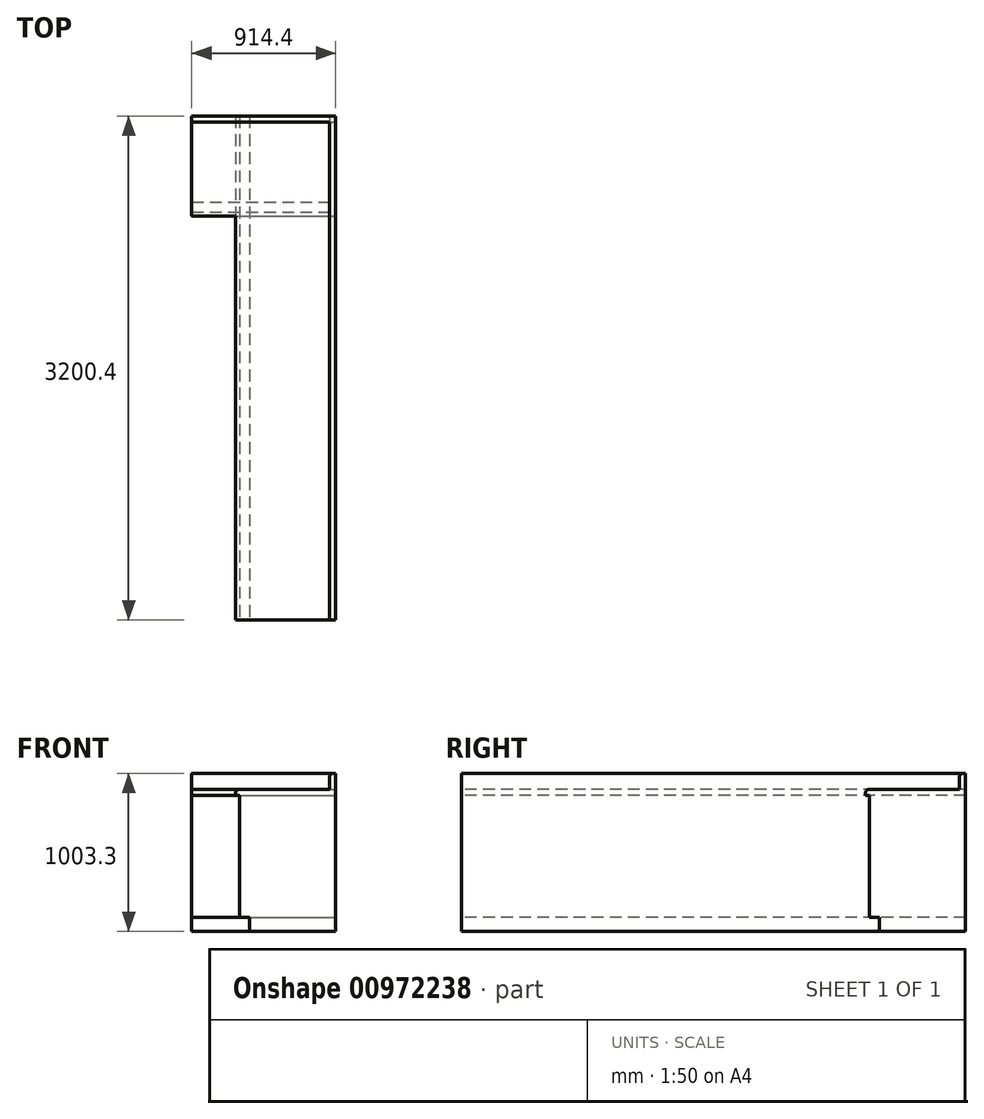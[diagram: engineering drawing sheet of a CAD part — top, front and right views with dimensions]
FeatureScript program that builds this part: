
annotation { "Feature Type Name" : "Feature", "Feature Type Description" : "" }
export const myFeature = defineFeature(function(context is Context, id is Id, definition is map)
    precondition{}
    {
        {
            var Q0;
            Q0=qCreatedBy(makeId("Front.planeOp"),FACE);
            var sketch = newSketch(context, id + "F0", { "sketchPlane" : qUnion([Q0])});
            skLineSegment(sketch, "E0", {"start": v(0, 0) * mm, "end": v(0, 1003.3) * mm});
            skLineSegment(sketch, "E1", {"start": v(0, 1003.3) * mm, "end": v(-19.05, 1003.3) * mm});
            skLineSegment(sketch, "E2", {"start": v(0, 0) * mm, "end": v(-546.1, 0) * mm});
            skLineSegment(sketch, "E3", {"start": v(-546.1, 0) * mm, "end": v(-546.1, 88.9) * mm});
            skLineSegment(sketch, "E4", {"start": v(-546.1, 88.9) * mm, "end": v(-609.6, 88.9) * mm});
            skLineSegment(sketch, "E5", {"start": v(-609.6, 88.9) * mm, "end": v(-609.6, 863.6) * mm});
            skLineSegment(sketch, "E6", {"start": v(-609.6, 863.6) * mm, "end": v(-635, 863.6) * mm});
            skLineSegment(sketch, "E7", {"start": v(-635, 863.6) * mm, "end": v(-635, 882.65) * mm});
            skArc(sketch, "E8", {"start": v(-615.95, 901.7) * mm, "mid": v(-629.42, 896.12) * mm, "end": v(-635, 882.65) * mm});
            skArc(sketch, "E9", {"start": v(-19.05, 1003.3) * mm, "mid": v(-32.52, 997.72) * mm, "end": v(-38.1, 984.25) * mm});
            skLineSegment(sketch, "E10", {"start": v(-38.1, 984.25) * mm, "end": v(-38.1, 901.7) * mm});
            skLineSegment(sketch, "E11", {"start": v(-38.1, 901.7) * mm, "end": v(-615.95, 901.7) * mm});
            skSolve(sketch);
        }
        {
            var Q0;
            Q0=makeQuery(id+"F0.imprint","IMPRINT",FACE,{"disambiguationData":[TD([[makeQuery(id+"F0.imprint","IMPRINT",EDGE,{"derivedFrom":sQuery(id+"F0.wireOp",EDGE,"E0")}),1.0]])]});
            extrude(context, id + "F1", {"entities" : qUnion([Q0]), "oppositeDirection" : true, "depth" : 3200.4 * mm, "offsetDistance" : 25.4 * mm});
        }
        {
            var Q0;
            Q0=makeQuery(id+"F1.opExtrude","CAP_FACE",FACE,{"disambiguationData":[OSD([sQuery(id+"F0.wireOp",EDGE,"E0"),sQuery(id+"F0.wireOp",EDGE,"E1"),sQuery(id+"F0.wireOp",EDGE,"E2"),sQuery(id+"F0.wireOp",EDGE,"E3"),sQuery(id+"F0.wireOp",EDGE,"E4"),sQuery(id+"F0.wireOp",EDGE,"E5"),sQuery(id+"F0.wireOp",EDGE,"E6"),sQuery(id+"F0.wireOp",EDGE,"E7"),sQuery(id+"F0.wireOp",EDGE,"E8"),sQuery(id+"F0.wireOp",EDGE,"E9"),sQuery(id+"F0.wireOp",EDGE,"E10"),sQuery(id+"F0.wireOp",EDGE,"E11")])],"isStart":false});
            extrude(context, id + "F2", {"entities" : qUnion([Q0]), "depth" : 914.4 * mm, "offsetDistance" : 25.4 * mm});
        }
        {
            var Q0;
            Q0=makeQuery(id+"F2.opExtrude","SWEPT_BODY",BODY,{"disambiguationData":[OSD([sQuery(id+"F0.wireOp",EDGE,"E0"),sQuery(id+"F0.wireOp",EDGE,"E1"),sQuery(id+"F0.wireOp",EDGE,"E2"),sQuery(id+"F0.wireOp",EDGE,"E3"),sQuery(id+"F0.wireOp",EDGE,"E4"),sQuery(id+"F0.wireOp",EDGE,"E5"),sQuery(id+"F0.wireOp",EDGE,"E6"),sQuery(id+"F0.wireOp",EDGE,"E7"),sQuery(id+"F0.wireOp",EDGE,"E8"),sQuery(id+"F0.wireOp",EDGE,"E9"),sQuery(id+"F0.wireOp",EDGE,"E10"),sQuery(id+"F0.wireOp",EDGE,"E11")])]});
            var Q1;
            Q1=makeQuery(id+"F1.opExtrude","CAP_EDGE",EDGE,{"disambiguationData":[OSD([sQuery(id+"F0.wireOp",EDGE,"E0")])],"isStart":false});
            circularPattern(context, id + "F3", {"entities" : qUnion([Q0]), "axis" : qUnion([Q1]), "angle" : 90 * degree, "instanceCount" : 2, "equalSpace" : true});
        }
        {
            var Q0;
            Q0=makeQuery(id+"F2.opExtrude","SWEPT_BODY",BODY,{"disambiguationData":[OSD([sQuery(id+"F0.wireOp",EDGE,"E0"),sQuery(id+"F0.wireOp",EDGE,"E1"),sQuery(id+"F0.wireOp",EDGE,"E2"),sQuery(id+"F0.wireOp",EDGE,"E3"),sQuery(id+"F0.wireOp",EDGE,"E4"),sQuery(id+"F0.wireOp",EDGE,"E5"),sQuery(id+"F0.wireOp",EDGE,"E6"),sQuery(id+"F0.wireOp",EDGE,"E7"),sQuery(id+"F0.wireOp",EDGE,"E8"),sQuery(id+"F0.wireOp",EDGE,"E9"),sQuery(id+"F0.wireOp",EDGE,"E10"),sQuery(id+"F0.wireOp",EDGE,"E11")])]});
            deleteBodies(context, id + "F4", {"entities" : qUnion([Q0])});
        }
    });
